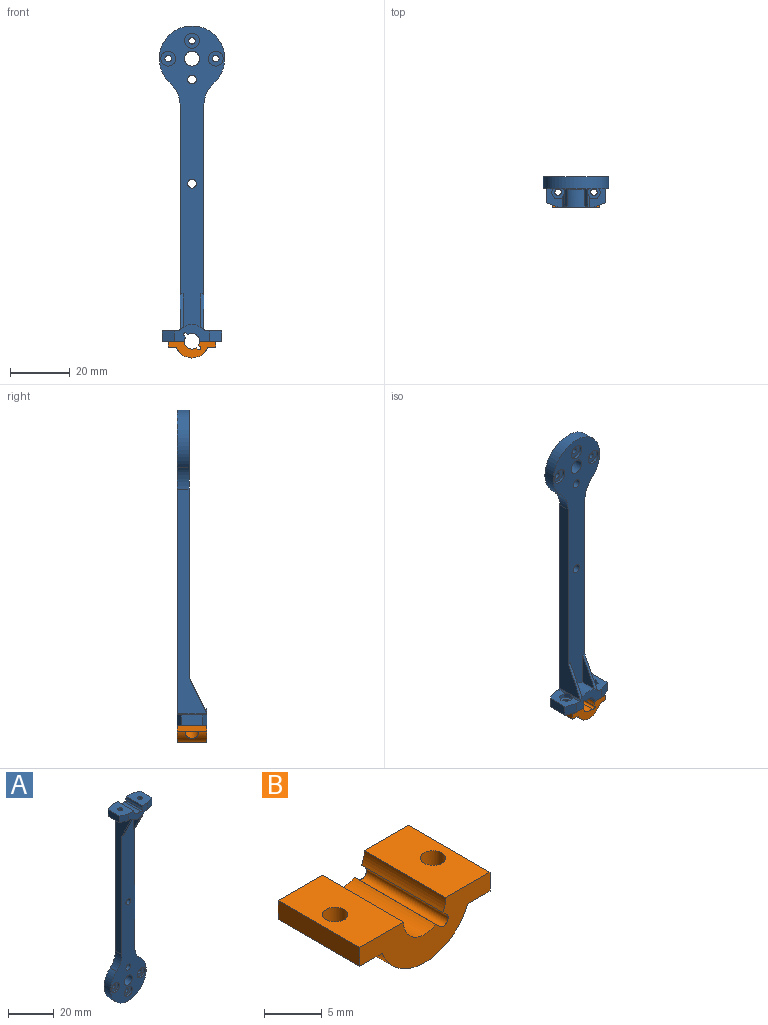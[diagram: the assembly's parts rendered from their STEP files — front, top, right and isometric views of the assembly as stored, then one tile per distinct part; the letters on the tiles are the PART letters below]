
ASSEMBLY  parts=2 mates=1
PART A: 62 faces, bbox 22x10x106 mm
  f0: cylinder r=2.6mm len=10mm, axis (0,1,0), area 14.4mm2, adj f16,f31,f32,f58
  f1: cylinder r=5.6mm len=4.36mm, axis (0,1,0), area 2.3mm2, adj f4,f24,f29,f32
  f2: cylinder r=5.6mm len=4.36mm, axis (0,1,0), area 2.3mm2, adj f5,f16,f24,f29
  f3: plane 101.27x22mm, normal (0,-1,0), area 905.2mm2, adj f10,f12,f17,f19,f21,f23,f24,f25
  f4: plane 2.07x1.94mm, normal (0.87,0.5,0), area 4mm2, adj f1,f5,f29,f45,f47,f50
  f5: plane 2.07x1.94mm, normal (0.87,-0.5,0), area 4mm2, adj f2,f4,f29,f45,f48,f50
  f6: cylinder r=1.1mm len=2.2mm, axis (0,0,1), area 13.8mm2, adj f31,f45
  f7: cylinder r=5.6mm len=4.36mm, axis (0,1,0), area 2.3mm2, adj f9,f16,f25,f36
  f8: cylinder r=5.6mm len=4.36mm, axis (0,1,0), area 2.3mm2, adj f9,f25,f32,f37
  f9: plane 10x5.63mm, normal (0,0,-1), area 36.8mm2, adj f7,f8,f16,f28,f32,f33,f34,f35
  f10: cylinder r=5.6mm len=8mm, axis (0,1,0), area 38.5mm2, adj f3,f32,f43,f44,f51,f52
  f11: cylinder r=1.1mm len=2.2mm, axis (0,0,1), area 13.8mm2, adj f27,f39
  f12: cylinder r=11mm len=22mm, axis (0,1,0), area 212.2mm2, adj f3,f16,f40,f41
  f13: cylinder r=1.1mm len=3mm, axis (0,1,0), area 20.7mm2, adj f16,f22
  f14: cylinder r=1.1mm len=3mm, axis (0,1,0), area 20.7mm2, adj f16,f20
  f15: cylinder r=1.1mm len=3mm, axis (0,1,0), area 20.7mm2, adj f16,f18
  f16: plane 106x22mm, normal (0,1,0), area 1018.7mm2, adj f0,f2,f7,f9,f12,f13,f14,f15
  f17: cylinder r=2.5mm len=5mm, axis (0,1,0), area 62.8mm2, adj f3,f16
  f18: plane 5x5mm, normal (0,-1,0), area 15.8mm2, adj f15,f19
  f19: cylinder r=2.5mm len=5mm, axis (0,-1,0), area 15.7mm2, adj f3,f18
  f20: plane 5x5mm, normal (0,-1,0), area 15.8mm2, adj f14,f21
  f21: cylinder r=2.5mm len=5mm, axis (0,-1,0), area 15.7mm2, adj f3,f20
  f22: plane 5x5mm, normal (0,-1,0), area 15.8mm2, adj f13,f23
  f23: cylinder r=2.5mm len=5mm, axis (0,-1,0), area 15.7mm2, adj f3,f22
  f24: plane 75.43x10mm, normal (1,0,0), area 337.7mm2, adj f1,f2,f3,f16,f40,f50,f51
  f25: plane 75.43x10mm, normal (-1,0,0), area 337.7mm2, adj f3,f7,f8,f16,f41,f42,f43
  f26: cylinder r=2.6mm len=10mm, axis (0,1,0), area 55.2mm2, adj f16,f27,f32,f59
  f27: plane 10x7.4mm, normal (0,0,1), area 64.4mm2, adj f11,f16,f26,f28,f32,f53,f54
  f28: plane 7.09x3.5mm, normal (-1,0,0), area 24.8mm2, adj f9,f27,f53,f54
  f29: plane 10x5.63mm, normal (0,0,-1), area 36.8mm2, adj f1,f2,f4,f5,f16,f30,f32,f46
  f30: plane 7.09x3.5mm, normal (1,0,0), area 24.8mm2, adj f29,f31,f55,f56
  f31: plane 10x7.4mm, normal (0,0,1), area 64.4mm2, adj f0,f6,f16,f30,f32,f55,f56
  f32: plane 12x5.6mm, normal (0,-1,0), area 42.9mm2, adj f0,f1,f8,f9,f10,f26,f27,f29
  f33: plane 2.05x1.5mm, normal (0.87,0.5,0), area 3.6mm2, adj f9,f34,f38,f39
  f34: plane 2.05x1.5mm, normal (0.87,-0.5,0), area 3.6mm2, adj f9,f33,f35,f39
  f35: plane 2.37x1.5mm, normal (0,-1,0), area 3.6mm2, adj f9,f34,f36,f39
  f36: plane 2.07x1.94mm, normal (-0.87,-0.5,0), area 4mm2, adj f7,f9,f35,f37,f39,f42
  f37: plane 2.07x1.94mm, normal (-0.87,0.5,0), area 4mm2, adj f8,f9,f36,f38,f39,f42
  f38: plane 2.37x1.5mm, normal (0,1,0), area 3.6mm2, adj f9,f33,f37,f39
  f39: plane 4.73x4.1mm, normal (0,0,-1), area 10.8mm2, adj f11,f33,f34,f35,f36,f37,f38
  f40: cylinder r=10mm len=7.45mm, axis (0,1,0), area 33.6mm2, adj f3,f12,f16,f24
  f41: cylinder r=10mm len=7.45mm, axis (0,1,0), area 33.6mm2, adj f3,f12,f16,f25
  f42: plane 1.27x0.37mm, normal (0,0,1), area 0.2mm2, adj f25,f36,f37
  f43: plane 12x6mm, normal (0,-0.89,-0.45), area 12.9mm2, adj f3,f10,f25,f44
  f44: plane 11.19x5.6mm, normal (1,0,0), area 31.3mm2, adj f3,f10,f43
  f45: plane 4.73x4.1mm, normal (0,0,-1), area 10.8mm2, adj f4,f5,f6,f46,f47,f48,f49
  f46: plane 2.05x1.5mm, normal (-0.87,0.5,0), area 3.6mm2, adj f29,f45,f47,f49
  f47: plane 2.37x1.5mm, normal (0,1,0), area 3.6mm2, adj f4,f29,f45,f46
  f48: plane 2.37x1.5mm, normal (0,-1,0), area 3.6mm2, adj f5,f29,f45,f49
  f49: plane 2.05x1.5mm, normal (-0.87,-0.5,0), area 3.6mm2, adj f29,f45,f46,f48
  f50: plane 1.27x0.37mm, normal (0,0,1), area 0.2mm2, adj f4,f5,f24
  f51: plane 12x6mm, normal (0,-0.89,-0.45), area 12.9mm2, adj f3,f10,f24,f52
  f52: plane 11.19x5.6mm, normal (-1,0,0), area 31.3mm2, adj f3,f10,f51
  f53: plane 4x3.5mm, normal (-0.34,-0.94,0), area 14.9mm2, adj f9,f27,f28,f32
  f54: plane 4x3.5mm, normal (-0.34,0.94,0), area 14.9mm2, adj f9,f16,f27,f28
  f55: plane 4x3.5mm, normal (0.34,0.94,0), area 14.9mm2, adj f16,f29,f30,f31
  f56: plane 4x3.5mm, normal (0.34,-0.94,0), area 14.9mm2, adj f29,f30,f31,f32
  f57: cylinder r=0.6mm len=10mm, axis (0,1,0), area 18.8mm2, adj f16,f32,f58,f59
  f58: plane 10x0.47mm, normal (-0.71,0,-0.71), area 6.7mm2, adj f0,f16,f32,f57
  f59: plane 10x0.47mm, normal (0.71,0,0.71), area 6.7mm2, adj f16,f26,f32,f57
  f60: cylinder r=1.5mm len=4mm, axis (0,-1,0), area 37.7mm2, adj f3,f16
  f61: cylinder r=1.5mm len=4mm, axis (0,-1,0), area 37.7mm2, adj f3,f16
PART B: 18 faces, bbox 16x10x5.6 mm
  f0: cylinder r=2.6mm len=10mm, axis (0,1,0), area 55.2mm2, adj f1,f7,f12,f15
  f1: plane 16x5.6mm, normal (0,1,0), area 47.4mm2, adj f0,f3,f5,f6,f7,f8,f9,f10
  f2: cylinder r=1.1mm len=2.2mm, axis (0,0,1), area 13.8mm2, adj f7,f9
  f3: cylinder r=5.6mm len=10.46mm, axis (0,1,0), area 113.1mm2, adj f1,f9,f10,f12,f13,f14
  f4: cylinder r=1.1mm len=2.2mm, axis (0,0,1), area 13.8mm2, adj f5,f10
  f5: plane 10x5.4mm, normal (0,0,1), area 50.2mm2, adj f1,f4,f6,f11,f12
  f6: cylinder r=2.6mm len=10mm, axis (0,1,0), area 14.4mm2, adj f1,f5,f12,f17
  f7: plane 10x5.4mm, normal (0,0,1), area 50.2mm2, adj f0,f1,f2,f8,f12
  f8: plane 10x2mm, normal (-1,0,0), area 20mm2, adj f1,f7,f9,f12
  f9: plane 10x4.5mm, normal (0,0,-1), area 29.9mm2, adj f1,f2,f3,f8,f12,f14
  f10: plane 10x4.5mm, normal (0,0,-1), area 29.9mm2, adj f1,f3,f4,f11,f12,f13
  f11: plane 10x2mm, normal (1,0,0), area 20mm2, adj f1,f5,f10,f12
  f12: plane 16x5.6mm, normal (0,-1,0), area 47.4mm2, adj f0,f3,f5,f6,f7,f8,f9,f10
  f13: cylinder r=2.5mm len=4.76mm, axis (0,0,1), area 10.8mm2, adj f3,f10
  f14: cylinder r=2.5mm len=4.76mm, axis (0,0,1), area 10.8mm2, adj f3,f9
  f15: plane 10x0.47mm, normal (0.71,0,0.71), area 6.7mm2, adj f0,f1,f12,f16
  f16: cylinder r=0.6mm len=10mm, axis (0,-1,0), area 18.8mm2, adj f1,f12,f15,f17
  f17: plane 10x0.47mm, normal (-0.71,0,-0.71), area 6.7mm2, adj f1,f6,f12,f16
PLACE A rot(axis=(0,1,0),180deg) t=(17.44,-9,181.15)mm
PLACE B t=(17.44,-9,86.15)mm
MATE revolute A.f0 <-> B.f0  axis (0,1,0) through (17.44,-19,86.15)mm
